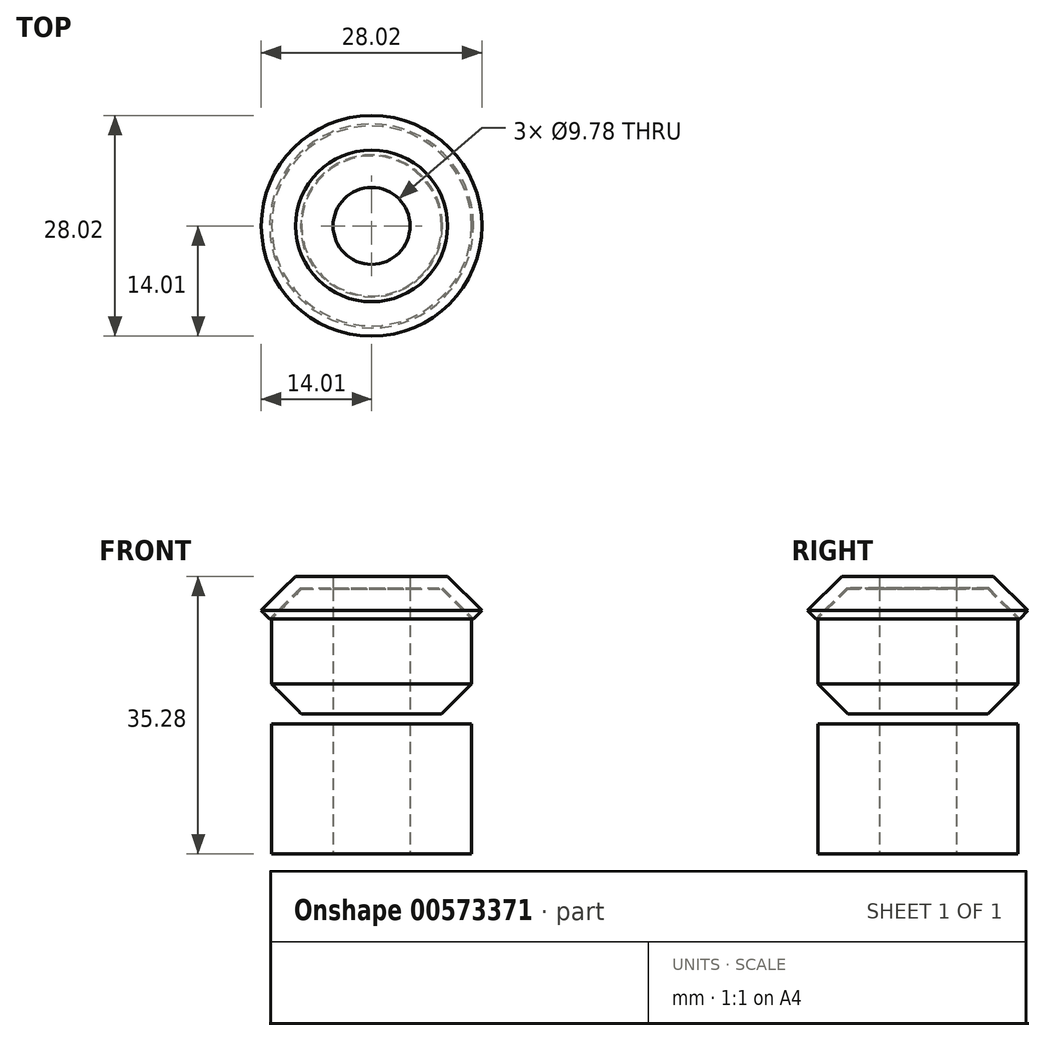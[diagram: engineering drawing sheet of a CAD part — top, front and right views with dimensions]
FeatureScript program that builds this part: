
annotation { "Feature Type Name" : "Feature", "Feature Type Description" : "" }
export const myFeature = defineFeature(function(context is Context, id is Id, definition is map)
    precondition{}
    {
        {
            var Q0;
            Q0=qCreatedBy(makeId("Front.planeOp"),FACE);
            var sketch = newSketch(context, id + "F0", { "sketchPlane" : qUnion([Q0])});
            skLineSegment(sketch, "E0", {"start": v(-22.39, 0) * mm, "end": v(31.52, 0) * mm, "construction": true});
            skLineSegment(sketch, "E1", {"start": v(0, -23.85) * mm, "end": v(0, 21.6) * mm, "construction": true});
            skLineSegment(sketch, "E2.bottom", {"start": v(4.89, -1.27) * mm, "end": v(12.7, -1.27) * mm});
            skLineSegment(sketch, "E2.top", {"start": v(4.89, -17.78) * mm, "end": v(12.7, -17.78) * mm});
            skLineSegment(sketch, "E2.left", {"start": v(4.89, -1.27) * mm, "end": v(4.89, -17.78) * mm});
            skLineSegment(sketch, "E2.right", {"start": v(12.7, -1.27) * mm, "end": v(12.7, -17.78) * mm});
            skLineSegment(sketch, "E3.bottom", {"start": v(4.89, 0) * mm, "end": v(8.9, 0) * mm});
            skLineSegment(sketch, "E3.top", {"start": v(4.89, 15.88) * mm, "end": v(8.9, 15.88) * mm});
            skLineSegment(sketch, "E3.left", {"start": v(4.89, 0) * mm, "end": v(4.89, 15.88) * mm});
            skLineSegment(sketch, "E3.right", {"start": v(12.7, 3.8) * mm, "end": v(12.7, 12.07) * mm});
            skLineSegment(sketch, "E4", {"start": v(8.9, 0) * mm, "end": v(12.7, 3.8) * mm});
            skLineSegment(sketch, "E5", {"start": v(8.9, 15.88) * mm, "end": v(12.7, 12.07) * mm});
            skLineSegment(sketch, "E6", {"start": v(4.89, 16) * mm, "end": v(9.02, 16) * mm});
            skLineSegment(sketch, "E7", {"start": v(9.02, 16) * mm, "end": v(12.95, 12.07) * mm});
            skLineSegment(sketch, "E8", {"start": v(12.95, 12.07) * mm, "end": v(14.01, 13.12) * mm});
            skLineSegment(sketch, "E9", {"start": v(14.01, 13.12) * mm, "end": v(9.64, 17.5) * mm});
            skLineSegment(sketch, "E10", {"start": v(9.64, 17.5) * mm, "end": v(4.89, 17.5) * mm});
            skLineSegment(sketch, "E11", {"start": v(4.89, 17.5) * mm, "end": v(4.89, 16) * mm});
            skSolve(sketch);
        }
        {
            var Q0;
            Q0 = qSketchRegion(id + "F0", true);
            var Q1;
            Q1=sQuery(id+"F0.wireOp",EDGE,"E1");
            revolve(context, id + "F1", {"entities" : qUnion([Q0]), "axis" : qUnion([Q1]), "revolveType" : RevolveType.FULL});
        }
    });
